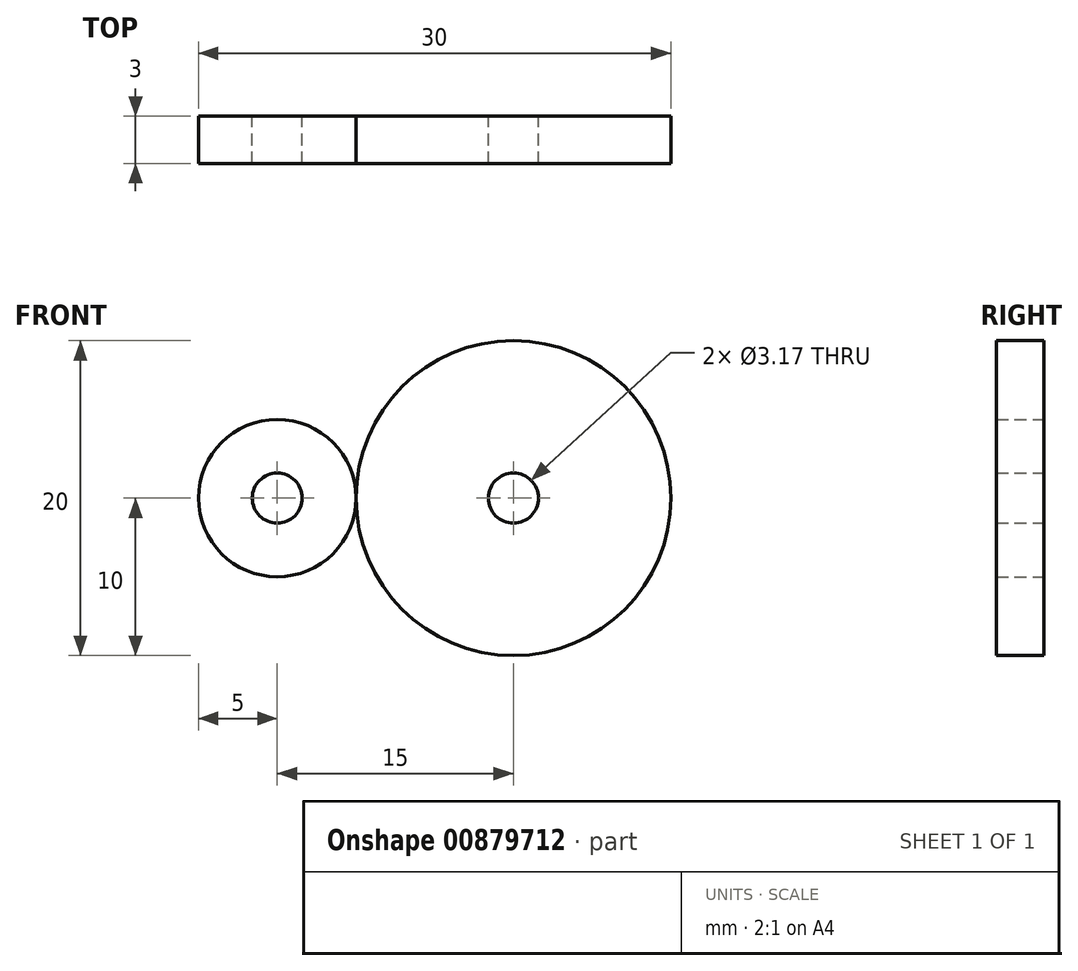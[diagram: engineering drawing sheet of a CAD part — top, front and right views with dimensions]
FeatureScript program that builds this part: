
annotation { "Feature Type Name" : "Feature", "Feature Type Description" : "" }
export const myFeature = defineFeature(function(context is Context, id is Id, definition is map)
    precondition{}
    {
        {
            var Q0;
            Q0=qCreatedBy(makeId("Front.planeOp"),FACE);
            var sketch = newSketch(context, id + "F0", { "sketchPlane" : qUnion([Q0])});
            skCircle(sketch, "E0", {"center": v(0, 0) * mm, "radius": 5 * mm});
            skCircle(sketch, "E1", {"center": v(15, 0) * mm, "radius": 10 * mm});
            skLineSegment(sketch, "E2", {"start": v(0, 0) * mm, "end": v(15, 0) * mm});
            skCircle(sketch, "E3", {"center": v(15, 0) * mm, "radius": 1.59 * mm});
            skCircle(sketch, "E4", {"center": v(0, 0) * mm, "radius": 1.59 * mm});
            skSolve(sketch);
        }
        {
            var Q0;
            Q0=makeQuery(id+"F0.imprint","IMPRINT",FACE,{"disambiguationData":[TD([[makeQuery(id+"F0.imprint","IMPRINT",EDGE,{"derivedFrom":sQuery(id+"F0.wireOp",EDGE,"E1")}),1.0]])]});
            var Q1;
            Q1=makeQuery(id+"F0.imprint","IMPRINT",FACE,{"disambiguationData":[TD([[makeQuery(id+"F0.imprint","IMPRINT",EDGE,{"derivedFrom":sQuery(id+"F0.wireOp",EDGE,"E0")}),1.0]])]});
            extrude(context, id + "F1", {"entities" : qUnion([Q0, Q1]), "depth" : 3 * mm, "offsetDistance" : 25.4 * mm});
        }
    });
